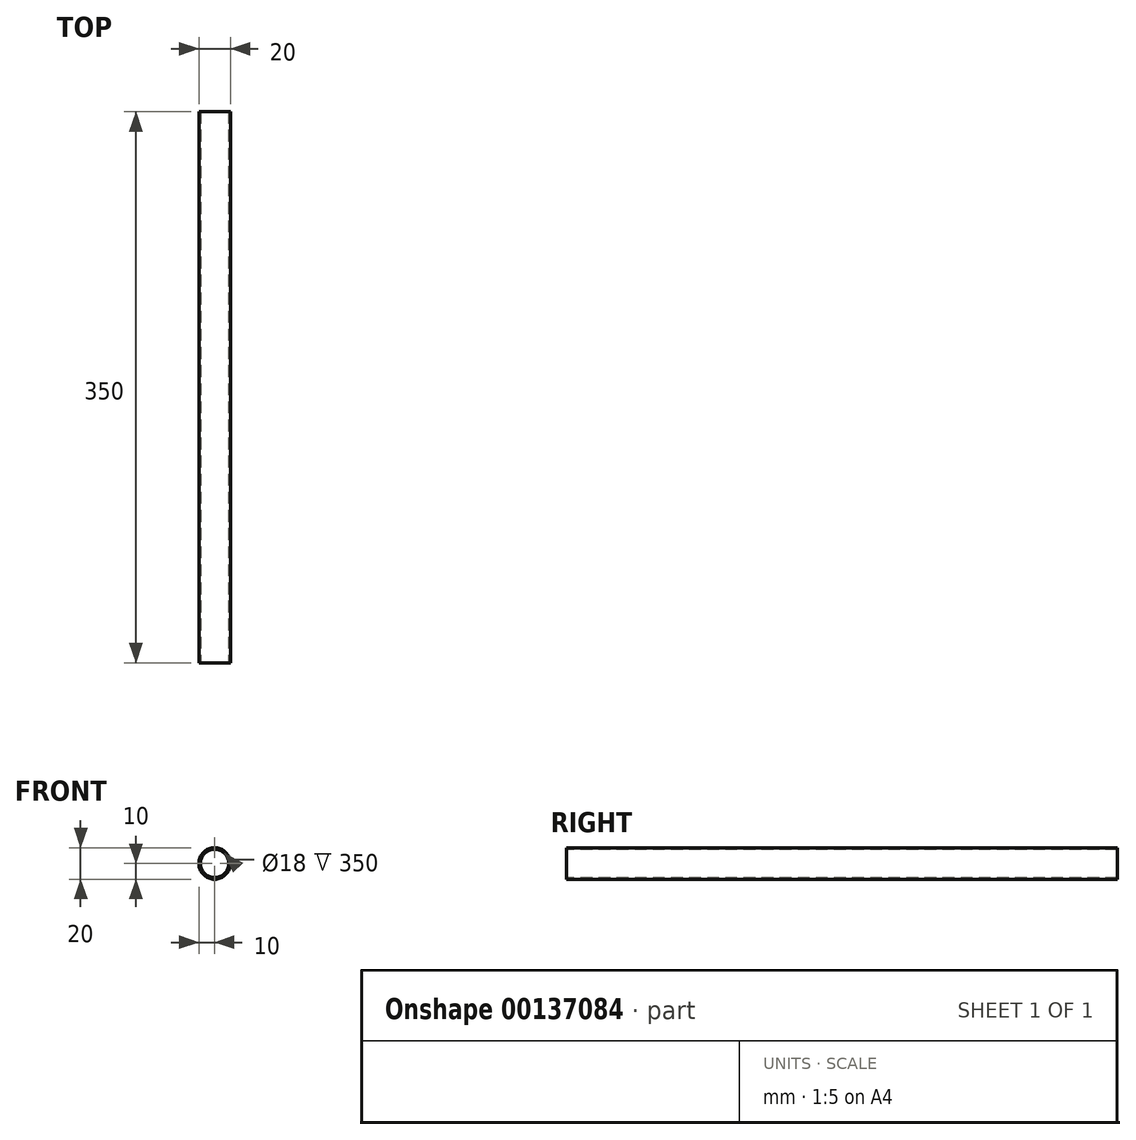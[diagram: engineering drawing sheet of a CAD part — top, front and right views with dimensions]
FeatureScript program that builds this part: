
annotation { "Feature Type Name" : "Feature", "Feature Type Description" : "" }
export const myFeature = defineFeature(function(context is Context, id is Id, definition is map)
    precondition{}
    {
        {
            var Q0;
            Q0=qCreatedBy(makeId("Front.planeOp"),FACE);
            var sketch = newSketch(context, id + "F0", { "sketchPlane" : qUnion([Q0])});
            skCircle(sketch, "E0", {"center": v(0, 0) * mm, "radius": 9 * mm});
            skCircle(sketch, "E1", {"center": v(0, 0) * mm, "radius": 10 * mm});
            skSolve(sketch);
        }
        {
            var Q0;
            Q0=makeQuery(id+"F0.imprint","IMPRINT",FACE,{"disambiguationData":[TD([[makeQuery(id+"F0.imprint","IMPRINT",EDGE,{"derivedFrom":sQuery(id+"F0.wireOp",EDGE,"E0")}),-1.0]])]});
            extrude(context, id + "F1", {"entities" : qUnion([Q0]), "oppositeDirection" : true, "depth" : 350 * mm});
        }
    });
